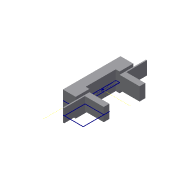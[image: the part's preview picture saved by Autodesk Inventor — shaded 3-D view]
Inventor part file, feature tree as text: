
AUTODESK INVENTOR PART (.ipt)
format: ipt  version: 2016 SP2 (Build 200236200, 236)  size: 113,152 bytes
history: native  units: mm
features: extrude x2, sketch x1, mirror x1
ambient origin geometry x8: Origin, YZ Plane, XZ Plane, XY Plane, X Axis, Y Axis, Z Axis, Center Point
bodies: Body1 (feature_tree)
feature tree (4):
  sketch  "Sketch1"  dims[d4=80.0mm d5=153.0mm d6=34.0mm d7=10.0mm d8=50.0mm d9=0.0mm d10=70.0mm d11=55.0mm d12=53.0mm d13=3.0mm d14=35.0mm d15=0.0mm]
  extrude  "Extrusion3"  Depth=153.0mm
  extrude  "Extrusion4"  Depth=34.0mm
  mirror  "Mirror1"
